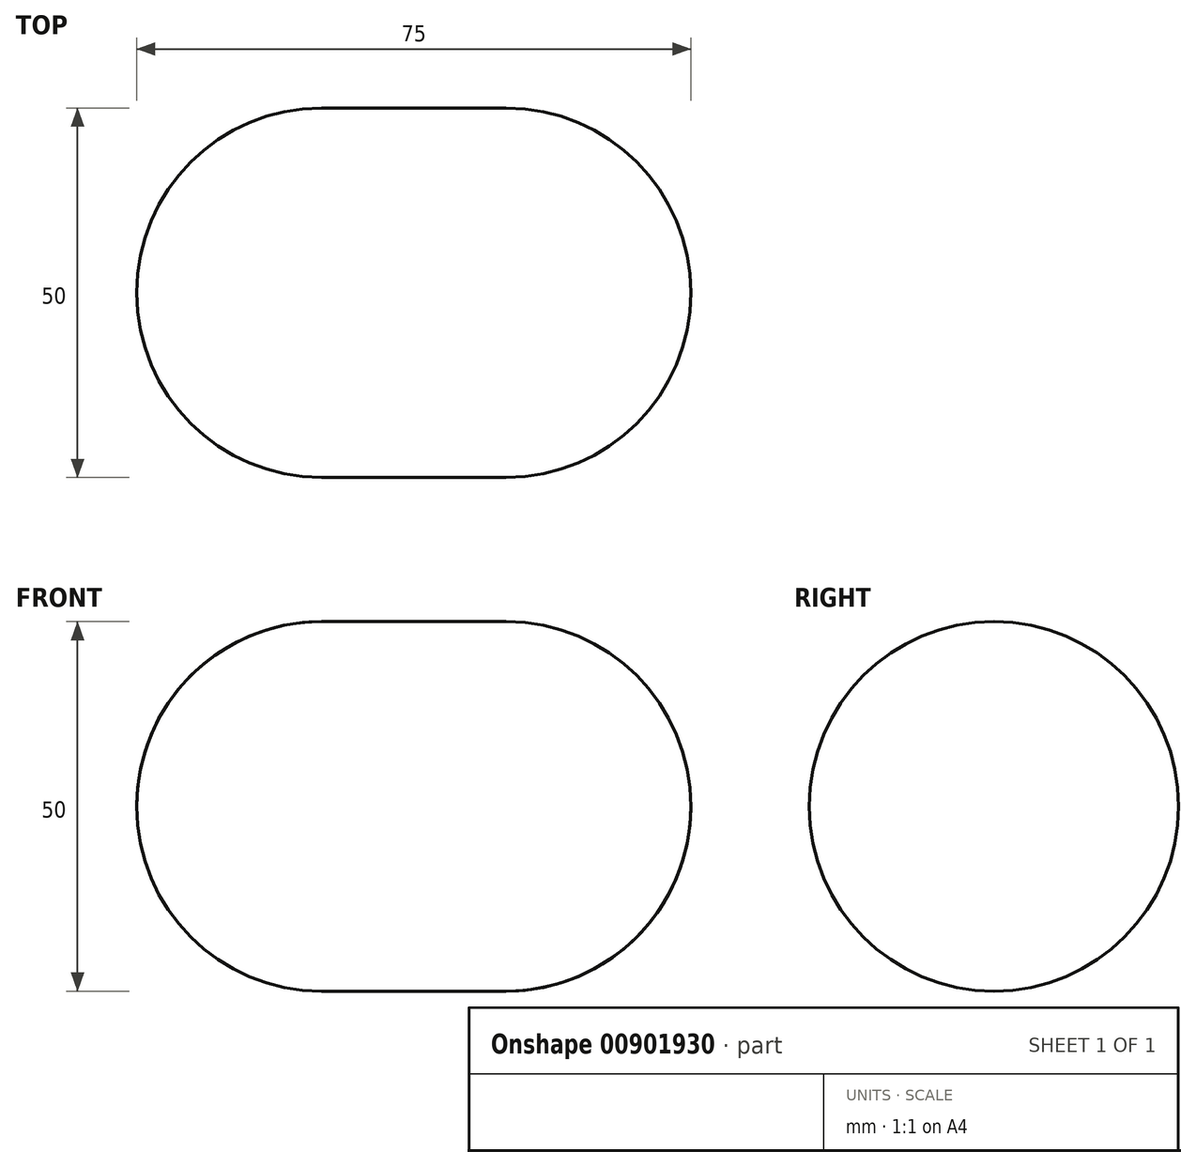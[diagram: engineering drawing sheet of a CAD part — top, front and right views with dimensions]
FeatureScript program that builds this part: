
annotation { "Feature Type Name" : "Feature", "Feature Type Description" : "" }
export const myFeature = defineFeature(function(context is Context, id is Id, definition is map)
    precondition{}
    {
        {
            var Q0;
            Q0=qCreatedBy(makeId("Front.planeOp"),FACE);
            var sketch = newSketch(context, id + "F0", { "sketchPlane" : qUnion([Q0])});
            skLineSegment(sketch, "E0.bottom", {"start": v(-12.5, 25) * mm, "end": v(12.5, 25) * mm});
            skLineSegment(sketch, "E0.top", {"start": v(-12.5, -25) * mm, "end": v(12.5, -25) * mm});
            skArc(sketch, "E1", {"start": v(-12.5, 25) * mm, "mid": v(-37.5, 0) * mm, "end": v(-12.5, -25) * mm});
            skArc(sketch, "E2", {"start": v(12.5, -25) * mm, "mid": v(37.5, 0) * mm, "end": v(12.5, 25) * mm});
            skLineSegment(sketch, "E3", {"start": v(-56.15, 0) * mm, "end": v(67.02, 0) * mm});
            skSolve(sketch);
        }
        {
            var Q0;
            {var subQ0=sQuery(id+"F0.wireOp",EDGE,"E0.bottom");Q0=makeQuery(id+"F0.imprint","IMPRINT",FACE,{"disambiguationData":[TD([[makeQuery(id+"F0.imprint","IMPRINT",EDGE,{"derivedFrom":subQ0}),-1.0]])]});}
            var Q1;
            Q1=sQuery(id+"F0.wireOp",EDGE,"E3");
            revolve(context, id + "F1", {"surfaceOperationType" : NewSurfaceOperationType.NEW, "entities" : qUnion([Q0]), "axis" : qUnion([Q1]), "revolveType" : RevolveType.FULL});
        }
    });
